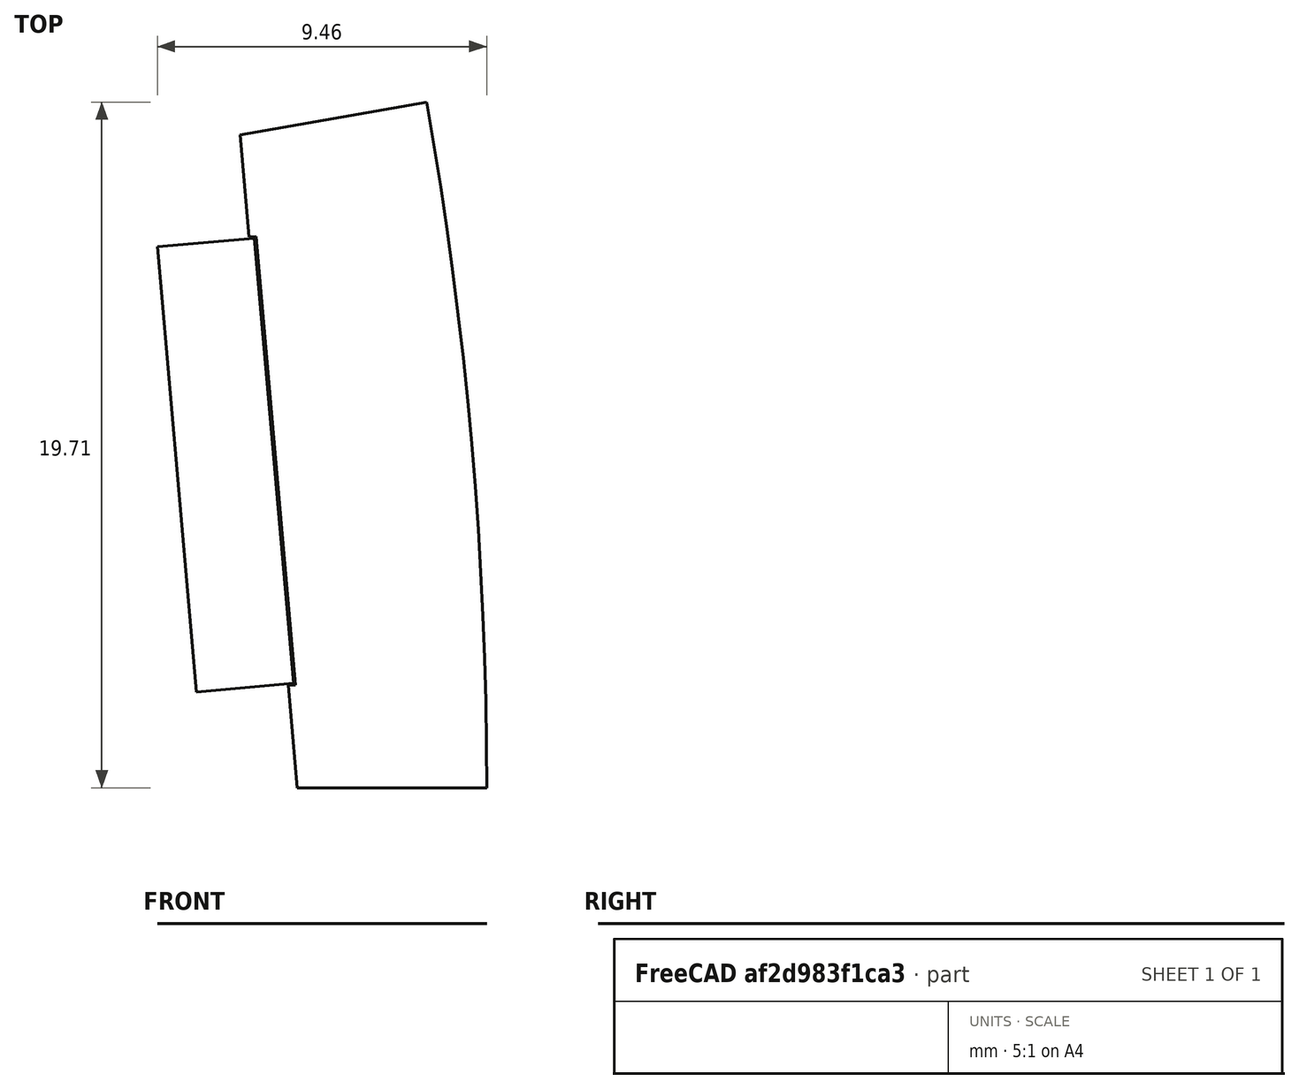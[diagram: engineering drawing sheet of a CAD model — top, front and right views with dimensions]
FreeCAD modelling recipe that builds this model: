
FCSTD DOCUMENT  (FreeCAD 0.18R4 (GitTag))
Label: RotorORBlockMagnetStraightBack
License: All rights reserved
LicenseURL: http://en.wikipedia.org/wiki/All_rights_reserved
objects: Sketcher::SketchObject×5, PartDesign::Body×2, Surface::Filling×2, Spreadsheet::Sheet×1
note: 9 computed .brp shape members not serialized (recipe doc carries the construction recipe); baked Part::Feature solids carry a one-line shape summary decoded from their .brp

FEATURE [Spreadsheet::Sheet] Spreadsheet  label="Variables"
  cells = A2=poleNumber; B2(poleNumber)=36; A3=outerDiameter; B3(outerDiameter)=227; D3=Calc Value; A4=innerDiameter; B4(innerDiameter)=210; D4=Input Value; A5=stackLength; B5(stackLength)=20; A6=stackingFactor; B6(stackingFactor)=0.95; A7=embrace; B7(embrace)=80; A8=contourRatio; B8(contourRatio)=80; A9=magnetAirgap; B9(magnetAirgap)=0.05; A10=poleSeparation; B10(poleSeparation)=2; A11=magnetWidth; B11(magnetWidth)=9; A12=magnetHeight; B12(magnetHeight)=2.8; A13=rib; B13(rib)=0.5; A14=bridgeCurved; B14(bridgeCurved)=0.5; A15=cutTop; B15(cutTop)=0.2; A16=cutBottom; B16(cutBottom)=0.25; A17=segmentAngle; B17(segmentAngle)==360 / poleNumber; A18=movePocketInwards; B18(movePocketInwards)=0.5; A19=cuttingThickness; B19(cuttingThickness)=0.1; A20=magnetLength; B20(magnetLength)==stackLength; A21=cut; B21(cut)=0.2; A22=ribShaft; B22(ribShaft)=0.5; A23=magnetEmbrace; B23(magnetEmbrace)=70; A24=magnetContourRatio; B24(magnetContourRatio)=90; A25=axialMisalignment; B25(axialMisalignment)=0.5
FEATURE [Sketcher::SketchObject] Sketch003  label="RotorSketch"
  MapMode = 5
  Support = -> [XY_Plane]
  expr: Constraints[60] = Variables.magnetAirgap
  expr: Constraints[51] = Variables.cut
  expr: Constraints[29] = Variables.segmentAngle * Variables.magnetEmbrace / 100
  expr: Constraints[15] = Variables.outerDiameter / 2
  expr: Constraints[50] = Variables.magnetAirgap
  expr: Constraints[36] = Variables.innerDiameter / 2 + Variables.magnetHeight + Variables.magnetAirgap
  expr: Constraints[18] = Variables.segmentAngle / 2
  expr: Constraints[0] = Variables.segmentAngle
  expr: Constraints[14] = Variables.innerDiameter / 2
  sketch-geometry (24):
    g0: LineSegment [constr] StartX=105 StartY=0 StartZ=0 EndX=113.5 EndY=0 EndZ=0
    g1: LineSegment [constr] StartX=103.405 StartY=18.2331 StartZ=0 EndX=111.776 EndY=19.7091 EndZ=0
    g2: LineSegment [constr] StartX=0 StartY=0 StartZ=0 EndX=105 EndY=0 EndZ=0
    g3: LineSegment [constr] StartX=0 StartY=0 StartZ=0 EndX=103.405 EndY=18.2331 EndZ=0
    g4: ArcOfCircle CenterX=0 CenterY=0 CenterZ=0 NormalX=0 NormalY=0 NormalZ=1 AngleXU=0 Radius=113.5 StartAngle=0 EndAngle=0.174533
    g5: ArcOfCircle [constr] CenterX=0 CenterY=0 CenterZ=0 NormalX=0 NormalY=0 NormalZ=1 AngleXU=0 Radius=105 StartAngle=0 EndAngle=0.174533
    g6: LineSegment [constr] StartX=0 StartY=0 StartZ=0 EndX=113.068 EndY=9.89218 EndZ=0
    g7: LineSegment [constr] StartX=103.8 StartY=18.3027 StartZ=0 EndX=105.401 EndY=0 EndZ=0
    g8: LineSegment [constr] StartX=104.041 StartY=15.549 StartZ=0 EndX=105.16 EndY=2.75372 EndZ=0
    g9: LineSegment [constr] StartX=0 StartY=0 StartZ=0 EndX=104.041 EndY=15.549 EndZ=0
    g10: LineSegment [constr] StartX=0 StartY=0 StartZ=0 EndX=105.16 EndY=2.75372 EndZ=0
    g11: LineSegment [constr] StartX=106.617 StartY=18.7995 StartZ=0 EndX=108.262 EndY=0 EndZ=0
    g12: LineSegment [constr] StartX=0 StartY=0 StartZ=0 EndX=107.44 EndY=9.39975 EndZ=0
    g13: LineSegment [constr] StartX=104.041 StartY=15.549 StartZ=0 EndX=106.88 EndY=15.7974 EndZ=0
    g14: LineSegment [constr] StartX=105.16 StartY=2.75372 StartZ=0 EndX=107.999 EndY=3.00211 EndZ=0
    g15: LineSegment StartX=106.876 StartY=15.8472 StartZ=0 EndX=106.676 EndY=15.8298 EndZ=0
    g16: LineSegment StartX=106.676 StartY=15.8298 StartZ=0 EndX=106.42 EndY=18.7646 EndZ=0
    g17: LineSegment [constr] StartX=106.876 StartY=15.8472 StartZ=0 EndX=106.88 EndY=15.7974 EndZ=0
    g18: LineSegment StartX=108.004 StartY=2.9523 StartZ=0 EndX=107.804 EndY=2.93487 EndZ=0
    g19: LineSegment StartX=107.804 StartY=2.93487 StartZ=0 EndX=108.061 EndY=0 EndZ=0
    g20: LineSegment [constr] StartX=108.004 StartY=2.9523 StartZ=0 EndX=107.999 EndY=3.00211 EndZ=0
    g21: LineSegment StartX=106.876 StartY=15.8472 StartZ=0 EndX=108.004 EndY=2.9523 EndZ=0
    g22: LineSegment StartX=106.42 StartY=18.7646 StartZ=0 EndX=111.776 EndY=19.7091 EndZ=0
    g23: LineSegment StartX=108.061 StartY=0 StartZ=0 EndX=113.5 EndY=0 EndZ=0
  constraints (67):
    c: Angle(g0,g1) = 0.174533
    c: Coincident(g2,g-1)
    c: Coincident(g2,g0)
    c: Coincident(g3,g2)
    c: Coincident(g3,g1)
    c: Parallel(g2,g0)
    c: Parallel(g3,g1)
    c: Coincident(g4,g-1)
    c: Coincident(g4,g0)
    c: Coincident(g4,g1)
    c: Coincident(g5,g4)
    c: Coincident(g5,g1)
    c: Coincident(g5,g0)
    c: Angle(g-1,g2) = 0
    c: Radius(g5) = 105
    c: Radius(g4) = 113.5
    c: Coincident(g6,g5)
    c: PointOnObject(g6,g4)
    c: Angle(g-1,g6) = 0.0872665
    c: PointOnObject(g7,g0)
    c: Tangent(g7,g5)
    c: Angle(g6,g7) = 1.5708
    c: PointOnObject(g7,g1)
    c: PointOnObject(g8,g7)
    c: Symmetric(g8,g8,g6)
    c: Coincident(g9,g5)
    c: Coincident(g9,g8)
    c: Coincident(g10,g5)
    c: Coincident(g10,g8)
    c: Angle(g10,g9) = 0.122173
    c: PointOnObject(g11,g1)
    c: PointOnObject(g11,g0)
    c: Angle(g11,g6) = 1.5708
    c: Coincident(g12,g-1)
    c: PointOnObject(g12,g11)
    c: Perpendicular(g12,g11)
    c: Distance(g12) = 107.85
    c: Coincident(g13,g8)
    c: PointOnObject(g13,g11)
    c: Coincident(g14,g8)
    c: PointOnObject(g14,g11)
    c: Angle(g11,g14) = 1.5708
    c: Angle(g13,g11) = 1.5708
    c: PointOnObject(g15,g11)
    c: Coincident(g16,g15)
    c: PointOnObject(g16,g1)
    c: Angle(g15,g16) = 1.5708
    c: Angle(g15,g11) = 1.5708
    c: Coincident(g17,g15)
    c: Coincident(g17,g13)
    c: Distance(g17) = 0.05
    c: Distance(g15) = 0.2
    c: PointOnObject(g18,g11)
    c: Coincident(g19,g18)
    c: PointOnObject(g19,g0)
    c: Parallel(g18,g14)
    c: Angle(g19,g18) = 1.5708
    c: Equal(g18,g15)
    c: Coincident(g20,g18)
    c: Coincident(g20,g14)
    c: Distance(g20) = 0.05
    c: Coincident(g21,g15)
    c: Coincident(g21,g18)
    c: Coincident(g22,g16)
    c: Coincident(g22,g1)
    c: Coincident(g23,g19)
    c: Coincident(g23,g0)
FEATURE [Sketcher::SketchObject] Sketch004  label="BoundingBox"
  MapMode = 5
  Support = -> [XY_Plane]
  expr: Constraints[8] = Variables.outerDiameter
  sketch-geometry (6):
    g0: LineSegment StartX=-113.5 StartY=-113.5 StartZ=0 EndX=113.5 EndY=-113.5 EndZ=0
    g1: LineSegment StartX=113.5 StartY=-113.5 StartZ=0 EndX=113.5 EndY=113.5 EndZ=0
    g2: LineSegment StartX=113.5 StartY=113.5 StartZ=0 EndX=-113.5 EndY=113.5 EndZ=0
    g3: LineSegment StartX=-113.5 StartY=113.5 StartZ=0 EndX=-113.5 EndY=-113.5 EndZ=0
    g4: LineSegment [constr] StartX=-113.5 StartY=-113.5 StartZ=0 EndX=113.5 EndY=113.5 EndZ=0
    g5: GeomPoint X=4.4e-15 Y=-1.8e-15 Z=0
  constraints (14):
    c: Coincident(g0,g1)
    c: Coincident(g1,g2)
    c: Coincident(g2,g3)
    c: Coincident(g3,g0)
    c: Horizontal(g0)
    c: Horizontal(g2)
    c: Vertical(g1)
    c: Vertical(g3)
    c: DistanceY(g1,g1) = 227
    c: Equal(g2,g1)
    c: Coincident(g4,g0)
    c: Coincident(g4,g1)
    c: Symmetric(g0,g1,g5)
    c: Coincident(g-1,g5)
FEATURE [Sketcher::SketchObject] Sketch005  label="RotorSideSketch"
  MapMode = 5
  Support = -> [XY_Plane001]
  expr: Constraints[22] = Variables.stackLength / 2 - Variables.axialMisalignment
  expr: Constraints[9] = Variables.outerDiameter / 2
  expr: Constraints[8] = Variables.innerDiameter / 2
  expr: Constraints[7] = Variables.stackLength
  sketch-geometry (8):
    g0: LineSegment StartX=-9.5 StartY=105 StartZ=0 EndX=10.5 EndY=105 EndZ=0
    g1: LineSegment StartX=10.5 StartY=105 StartZ=0 EndX=10.5 EndY=113.5 EndZ=0
    g2: LineSegment StartX=10.5 StartY=113.5 StartZ=0 EndX=-9.5 EndY=113.5 EndZ=0
    g3: LineSegment StartX=-9.5 StartY=113.5 StartZ=0 EndX=-9.5 EndY=105 EndZ=0
    g4: LineSegment StartX=-9.5 StartY=-105 StartZ=0 EndX=10.5 EndY=-105 EndZ=0
    g5: LineSegment StartX=10.5 StartY=-105 StartZ=0 EndX=10.5 EndY=-113.5 EndZ=0
    g6: LineSegment StartX=10.5 StartY=-113.5 StartZ=0 EndX=-9.5 EndY=-113.5 EndZ=0
    g7: LineSegment StartX=-9.5 StartY=-113.5 StartZ=0 EndX=-9.5 EndY=-105 EndZ=0
  constraints (23):
    c: Coincident(g0,g1)
    c: Coincident(g1,g2)
    c: Coincident(g2,g3)
    c: Coincident(g3,g0)
    c: Horizontal(g0)
    c: Vertical(g1)
    c: Vertical(g3)
    c: DistanceX(g2,g2) = 20
    c: DistanceY(g-1,g0) = 105
    c: DistanceY(g-1,g1) = 113.5
    c: Coincident(g4,g5)
    c: Coincident(g5,g6)
    c: Coincident(g6,g7)
    c: Coincident(g7,g4)
    c: Horizontal(g4)
    c: Vertical(g5)
    c: Vertical(g7)
    c: Equal(g4,g0)
    c: Equal(g7,g3)
    c: Horizontal(g2)
    c: Horizontal(g6)
    c: Symmetric(g4,g0,g-1)
    c: DistanceX(g0,g-1) = 9.5
FEATURE [Sketcher::SketchObject] Sketch006  label="MagnetSideSketch"
  MapMode = 5
  Support = -> [XY_Plane001]
  expr: Constraints[20] = Variables.stackLength / 2 - Variables.axialMisalignment
  expr: Constraints[17] = Variables.innerDiameter / 2
  expr: Constraints[14] = Variables.stackLength
  expr: Constraints[3] = Variables.magnetHeight
  sketch-geometry (8):
    g0: LineSegment StartX=-9.5 StartY=105 StartZ=0 EndX=10.5 EndY=105 EndZ=0
    g1: LineSegment StartX=10.5 StartY=105 StartZ=0 EndX=10.5 EndY=107.8 EndZ=0
    g2: LineSegment StartX=-9.5 StartY=107.8 StartZ=0 EndX=-9.5 EndY=105 EndZ=0
    g3: LineSegment StartX=-9.5 StartY=-105 StartZ=0 EndX=10.5 EndY=-105 EndZ=0
    g4: LineSegment StartX=10.5 StartY=-105 StartZ=0 EndX=10.5 EndY=-107.8 EndZ=0
    g5: LineSegment StartX=10.5 StartY=-107.8 StartZ=0 EndX=-9.5 EndY=-107.8 EndZ=0
    g6: LineSegment StartX=-9.5 StartY=-107.8 StartZ=0 EndX=-9.5 EndY=-105 EndZ=0
    g7: LineSegment StartX=-9.5 StartY=107.8 StartZ=0 EndX=10.5 EndY=107.8 EndZ=0
  constraints (23):
    c: Coincident(g0,g1)
    c: Coincident(g2,g0)
    c: Horizontal(g0)
    c: DistanceY(g1,g1) = 2.8
    c: Coincident(g3,g4)
    c: Coincident(g4,g5)
    c: Coincident(g5,g6)
    c: Coincident(g6,g3)
    c: Horizontal(g3)
    c: Vertical(g4)
    c: Vertical(g6)
    c: Equal(g6,g2)
    c: Coincident(g7,g2)
    c: Coincident(g7,g1)
    c: DistanceX(g7,g7) = 20
    c: Horizontal(g5)
    c: Equal(g6,g1)
    c: DistanceY(g-1,g0) = 105
    c: Symmetric(g0,g3,g-1)
    c: Equal(g5,g7)
    c: DistanceX(g0,g-1) = 9.5
    c: Angle(g0,g2) = 1.5708
    c: Angle(g1,g0) = 1.5708
FEATURE [PartDesign::Body] Body001  label="SideView"
  Group = -> [Sketch005,Sketch006]
  Origin = -> Origin001
FEATURE [Sketcher::SketchObject] Sketch  label="MagnetSketch"
  ExternalGeometry = -> [Sketch003]
  MapMode = 5
  Support = -> [XY_Plane]
  expr: Constraints[16] = Variables.magnetHeight
  expr: Constraints[14] = Variables.magnetAirgap
  sketch-geometry (7):
    g0: LineSegment StartX=104.041 StartY=15.549 StartZ=0 EndX=106.83 EndY=15.793 EndZ=0
    g1: LineSegment StartX=106.83 StartY=15.793 StartZ=0 EndX=107.95 EndY=2.99775 EndZ=0
    g2: LineSegment StartX=107.95 StartY=2.99775 StartZ=0 EndX=105.16 EndY=2.75372 EndZ=0
    g3: LineSegment StartX=105.16 StartY=2.75372 StartZ=0 EndX=104.041 EndY=15.549 EndZ=0
    g4: LineSegment [constr] StartX=106.83 StartY=15.793 StartZ=0 EndX=106.88 EndY=15.7974 EndZ=0
    g5: LineSegment [constr] StartX=106.83 StartY=15.793 StartZ=0 EndX=106.826 EndY=15.8428 EndZ=0
    g6: LineSegment [constr] StartX=107.95 StartY=2.99775 StartZ=0 EndX=107.954 EndY=2.94794 EndZ=0
  constraints (21):
    c: Coincident(g1,g0)
    c: Coincident(g2,g1)
    c: Coincident(g3,g2)
    c: Coincident(g3,g0)
    c: Angle(g1,g2) = 1.5708
    c: Equal(g0,g2)
    c: Parallel(g3,g1)
    c: Coincident(g4,g0)
    c: PointOnObject(g4,g-4)
    c: Coincident(g5,g0)
    c: PointOnObject(g5,g-3)
    c: Angle(g4,g5) = 1.5708
    c: Equal(g4,g5)
    c: Angle(g1,g4) = 1.5708
    c: Distance(g4) = 0.05
    c: Parallel(g1,g-4)
    c: Distance(g2) = 2.8
    c: Coincident(g6,g1)
    c: PointOnObject(g6,g-5)
    c: Angle(g2,g6) = 1.5708
    c: Equal(g6,g5)
FEATURE [PartDesign::Body] Body  label="TopView"
  Group = -> [Sketch003,Sketch004,Sketch]
  Origin = -> Origin
FEATURE [Surface::Filling] Surface  label="Magnet_Surface"
  Anisotropy = false
  BoundaryEdges = -> [Sketch]
  BoundaryOrder = [0,0,0,0]
  Degree = 3
  Iterations = 2
  MaximumDegree = 8
  MaximumSegments = 9
  PointsOnCurve = 15
  TolAngular = 0.01
  TolCurvature = 0.1
  Tolerance2d = 1e-05
  Tolerance3d = 0.0001
FEATURE [Surface::Filling] Surface001  label="Rotor_Surface"
  Anisotropy = false
  BoundaryEdges = -> [Sketch003]
  BoundaryOrder = [0,0,0,0,0,0,0,0]
  Degree = 3
  Iterations = 2
  MaximumDegree = 8
  MaximumSegments = 9
  PointsOnCurve = 15
  TolAngular = 0.01
  TolCurvature = 0.1
  Tolerance2d = 1e-05
  Tolerance3d = 0.0001
